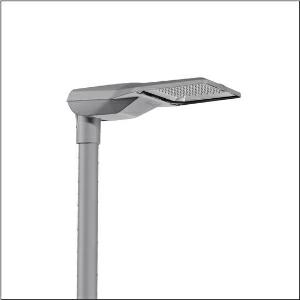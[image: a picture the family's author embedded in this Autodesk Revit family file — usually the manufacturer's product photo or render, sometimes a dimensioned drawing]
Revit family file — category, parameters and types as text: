
# Revit family: streetlight_sl_21_iq_midi___st1_0a_5xe3d21g08nb_5ac0
name_source: partatom
category: Lighting Fixtures
units: mm (PartAtom-declared; Revit-internal decimal feet)

## family parameters
Cut with Voids When Loaded = No
Host = Face
Light Source = No
Part Type = Normal
Room Calculation Point = No
Round Connector Dimension = Use Diameter
Shared = No

## types (1)
- --- (1 x LED, 19210 lm, 155.5 W, 2200K)
    Apparent Load = 155 VA
    CIE Flux Codes = 40 73 97 100 100
    Color Rendering = 70
    Color Temperature = 2200K
    Default Elevation = 1800 mm
    Description = Streetlight SL 21 iQ midi, mast luminaire, primary light control with lens, of PMMA, primary optical cover: cover, of toughened safety glass, transparent, light distribution: ST1.0a, light emission: direct distribution, primary light characteristic: asymmetric, installation type: post-top, side-entry, LED, High Power LED, rated luminous flux: 19.210lm, luminous efficacy: 124lm/W, light colour: 722, colour temperature: 2200K, control: Street-Remote, Auto-Match, Temp-Guard, Lumen-Switch, Night-Set, Smart-Wire, Light-Fading, Desk-Remote (wireless, voltage-free reading and setting of iQ features in the workshop via application-optimized NFC function/RFID function), optimised constant luminous flux control (CLO 2.0), presetting dimming linear, mains connection: 230..240V, AC, 50/60Hz, start of lifetime: 156W, end of service life: 162W, reduction: 69W, luminaire housing, of diecast aluminium, powder-coated, Siteco® metallic grey (DB 702S), corrosivity category C5 mid according to DIN EN ISO 12944, please order mast flange separately, inclination adjustable: 0°, 5°, 10°, 15°, sealing non-destructively replaceable, multi-level sealing system, length: 644mm, width: 335mm, height: 110mm, mast flange for spigot size: 42mm (side-entry): 5XC10008XM4, 60/48mm (side-entry/post-top): 5XC10108XM2, 76/60mm (side-entry/post-top): 5XC10108XM1, protection rating (complete): IP66, insulation class (complete): insulation class II (safety insulation), certification: CE, ENEC, ENEC+, VDE, impact resistance: IK09, permissible operating ambient temperature for outdoor applications: -40..+50°C, standard-compliant lighting for roads and squares, packaging unit: 1 piece

Light Distribution: ST1.0a
    Height = 111 mm
    Lamp = 1 x LED
    Lamp Light Flux = 19210 lm
    Lamp Power = 155.5 W
    Lamp count = 1
    Length = 644 mm
    Luminous efficacy = 124 lm/W
    Manufacturer = Siteco
    ModVariant = No
    Model = 5XE3D21G08NB
    Number of Poles = 1
    OnlyDefault = Yes
    Power Factor = 1
    Product Name = Streetlight SL 21 iQ midi | ST1.0a
    Product group = mast luminaire | pylon top
    ProductGroupID = 6100
    Protection Class = Protection class II
    Protection Degree = IP 66
    RLX_Detail_Level = 1
    RLX_Emergency_Light_Flux = 0 lm
    RLX_Emergency_Type = 0
    RLX_Emergency_Type_DB = No
    RlxData = <blob elided: 91833 chars, md5=8e4077f6>
    Socket = socket
    Standby Power = 0 W
    System Light Flux = 19210 lm
    System Power = 155 W
    Type Comments = factory setting: luminous flux: 100 % | dim-lin: 254 | 823 mA
    Type Image = l_1004298.jpg
    URL = http://relux.com
    VarID = @adj_103663
    Voltage = 0 V
    Weight = 0.00 kg
    Width = 336 mm

## geometry (parser evidence)
native form markers: Blend x4, Sweep x10
no freeform markers — native parametric forms only
